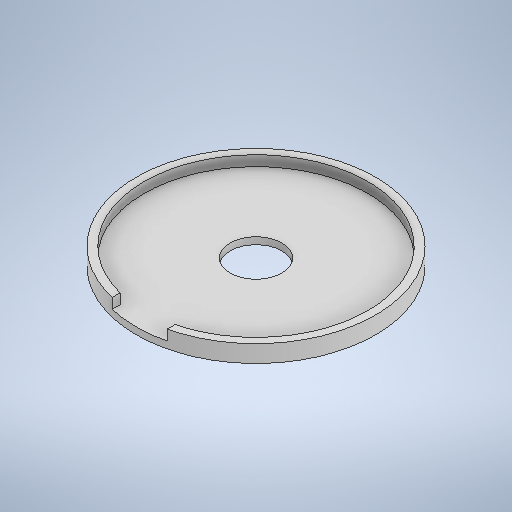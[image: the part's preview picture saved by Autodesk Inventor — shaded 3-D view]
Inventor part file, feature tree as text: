
AUTODESK INVENTOR PART (.ipt)
format: ipt  version: 2025.1 (Build 291241000, 241)  size: 265,216 bytes
history: native  units: mm
features: extrude x4, sketch x4
ambient origin geometry x8: Origin, YZ Plane, XZ Plane, XY Plane, X Axis, Y Axis, Z Axis, Center Point
bodies: Volumenkörper1 (feature_tree)
feature tree (8):
  extrude  "Extrusion1"  Depth=5.0mm TaperAngle=0.0deg
  extrude  "Extrusion2"  Depth=3.0mm TaperAngle=0.0deg
  extrude  "Extrusion3"  TaperAngle=0.0deg  [1 undecoded]
  extrude  "Extrusion4"  Depth=16.0mm
  sketch  "Skizze1"  dims[d0=69.55mm d1=5.0mm d2=0.0mm]
  sketch  "Skizze2"  dims[d3=65.08mm d4=3.0mm d5=0.0mm]
  sketch  "Skizze3"  dims[d6=15.12mm d7=0.0mm d8=0.0mm]
  sketch  "Skizze4"  dims[d9=16.0mm d10=16.0mm d11=10.0mm d12=0.0mm]
note: 1 required parameter value undecoded (feature->parameter linkage not recoverable at this tier; creation-order binding heuristic only, values carry confidence <= 0.55)
